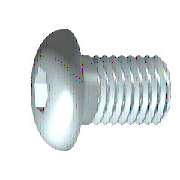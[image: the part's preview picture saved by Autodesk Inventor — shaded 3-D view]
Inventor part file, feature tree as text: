
AUTODESK INVENTOR PART (.ipt)
format: ipt  version: 2024.2 (Build 282272000, 272)  size: 197,120 bytes
history: native  units: mm (DEFAULTED — no unit token found)
features: extrude x1, plane x1, fillet x1
ambient origin geometry x7: Origin, YZ Plane, XY Plane, X Axis, Y Axis, Z Axis, Center Point
bodies: Solid1 (feature_tree), Body (feature_tree)
feature tree (3):
  extrude  "Slot"  Depth=8.5mm
  plane  "Work Plane1"
  fillet  "Fillet2"  Radius=0.306825mm
